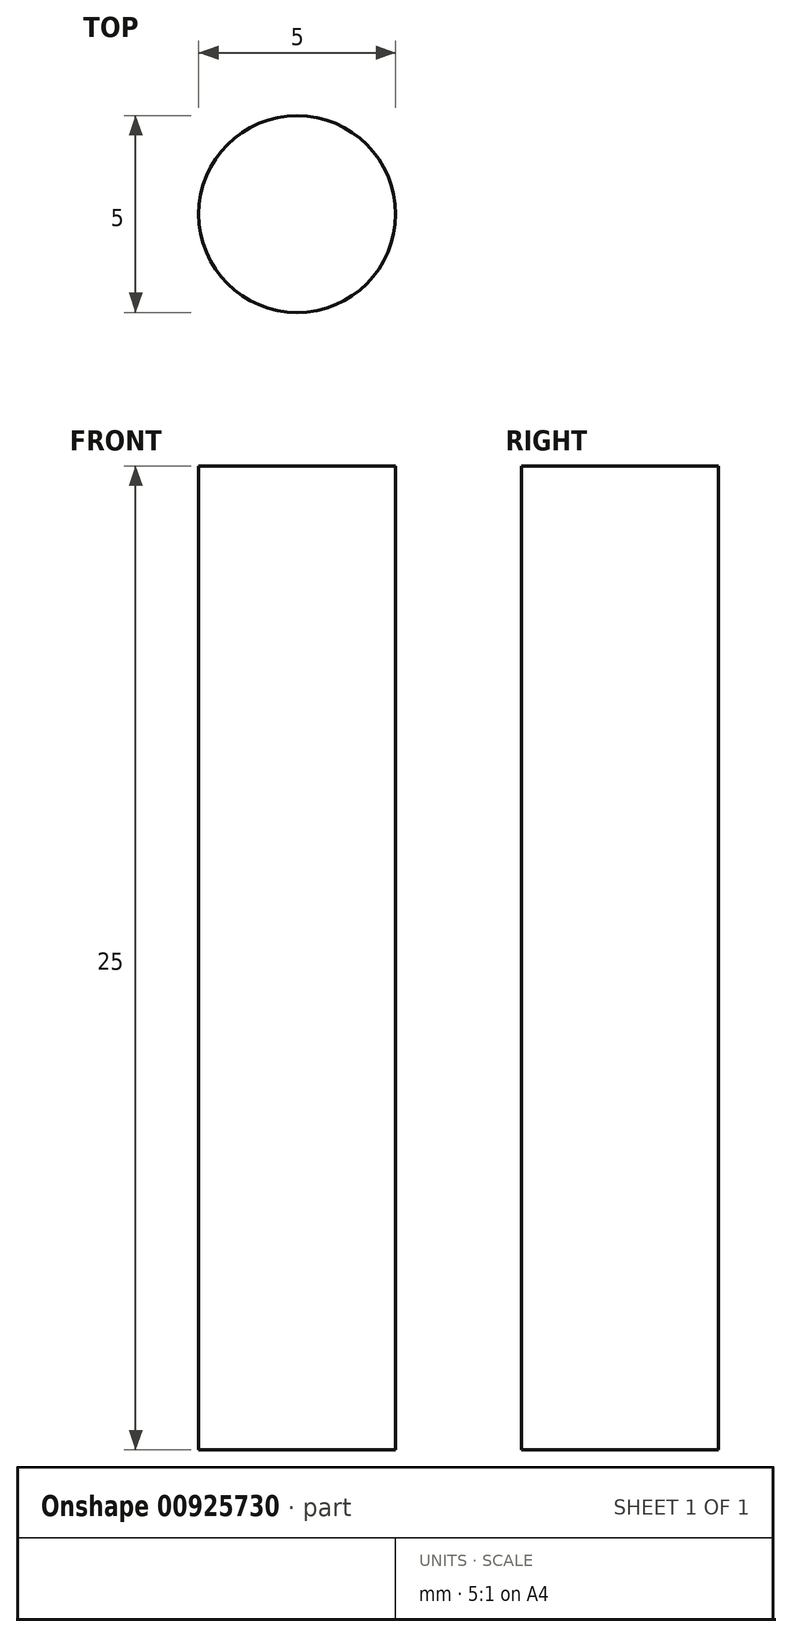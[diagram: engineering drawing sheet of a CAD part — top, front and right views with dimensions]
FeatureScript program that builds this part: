
annotation { "Feature Type Name" : "Feature", "Feature Type Description" : "" }
export const myFeature = defineFeature(function(context is Context, id is Id, definition is map)
    precondition{}
    {
        {
            var Q0;
            Q0=qCreatedBy(makeId("Top.planeOp"),FACE);
            var sketch = newSketch(context, id + "F0", { "sketchPlane" : qUnion([Q0])});
            skCircle(sketch, "E0", {"center": v(0, 0) * mm, "radius": 2.5 * mm});
            skSolve(sketch);
        }
        {
            var Q0;
            Q0=qSketchRegion(id+"F0",true);
            extrude(context, id + "F1", {"entities" : qUnion([Q0]), "depth" : 25 * mm, "offsetDistance" : 25 * mm});
        }
    });
